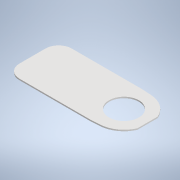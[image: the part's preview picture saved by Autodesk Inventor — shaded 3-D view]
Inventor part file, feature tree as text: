
AUTODESK INVENTOR PART (.ipt)
format: ipt  version: 2021 (Build 250183000, 183)  size: 124,928 bytes
history: native  units: mm
features: extrude x1, sketch x1
ambient origin geometry x8: Origin, YZ Plane, XZ Plane, XY Plane, X Axis, Y Axis, Z Axis, Center Point
bodies: Solid1 (feature_tree)
feature tree (2):
  extrude  "Extrusion1"  Depth=20.0mm
  sketch  "Sketch1"  dims[d0=11.4mm d1=9.0mm d2=12.65mm d6=5.0mm d8=0.5mm d9=0.0mm d10=20.0mm d11=19.6mm d12=4.0mm d13=20.0mm d14=20.0mm]
